# Revit family: Deckel für T-Abzweigstück Magic, Bei NB 300-600
name_source: partatom
category: Generic Models
revit_build: Autodesk Revit 2015 (Build: 20140606_1530(x64)
units: mm (PartAtom-declared; Revit-internal decimal feet)

## types (8) — shared parameters
Height = 1 mm  [stored 0.00328084 ft]
Height 1 = 2 mm  [stored 0.00656168 ft]
Length 1 = 5 mm  [stored 0.0164042 ft]
Manufacturer = OBO Bettermann
URL = http://www.obo-bettermann.com

## per-type parameters (varying)
| type | GTIN | Length | Length 2 | Manufacturer Art.No. | Material | Width | Width 1 |
| DFTM 300 FS | 4012195930914 | 351 mm | 304 mm  [stored 0.997375 ft] | 7138796 | Strip-galvanised | 397 mm | 199 mm |
| DFTM 400 FS | 4012195930921 | 451 mm  [stored 1.47966 ft] | 404 mm | 7138798 | Strip-galvanised | 497 mm | 249 mm |
| DFTM 500 FS | 4012195930938 | 551 mm  [stored 1.80774 ft] | 504 mm | 7138800 | Strip-galvanised | 597 mm | 299 mm |
| DFTM 600 FS | 4012195930945 | 651 mm  [stored 2.13583 ft] | 604 mm | 7138802 | Strip-galvanised | 697 mm | 349 mm |
| DFTM 300 DD | 4012195931010 | 351 mm | 304 mm  [stored 0.997375 ft] | 7138836 | Strip galvanised zinc/aluminium, Double Dip | 397 mm | 199 mm |
| DFTM 400 DD | 4012195931027 | 451 mm  [stored 1.47966 ft] | 404 mm | 7138838 | Strip galvanised zinc/aluminium, Double Dip | 497 mm | 249 mm |
| DFTM 500 DD | 4012195931058 | 551 mm  [stored 1.80774 ft] | 504 mm | 7138840 | Strip galvanised zinc/aluminium, Double Dip | 597 mm | 299 mm |
| DFTM 600 DD | 4012195931065 | 651 mm  [stored 2.13583 ft] | 604 mm | 7138842 | Strip galvanised zinc/aluminium, Double Dip | 697 mm | 349 mm |

note: column(s) folded — value = type name in every type: Article Type

note: [stored X ft] marks values corroborated as IEEE doubles in the binary element streams (Revit-internal decimal feet)

## geometry (parser evidence)
native form markers: Sweep x1
no freeform markers — native parametric forms only
